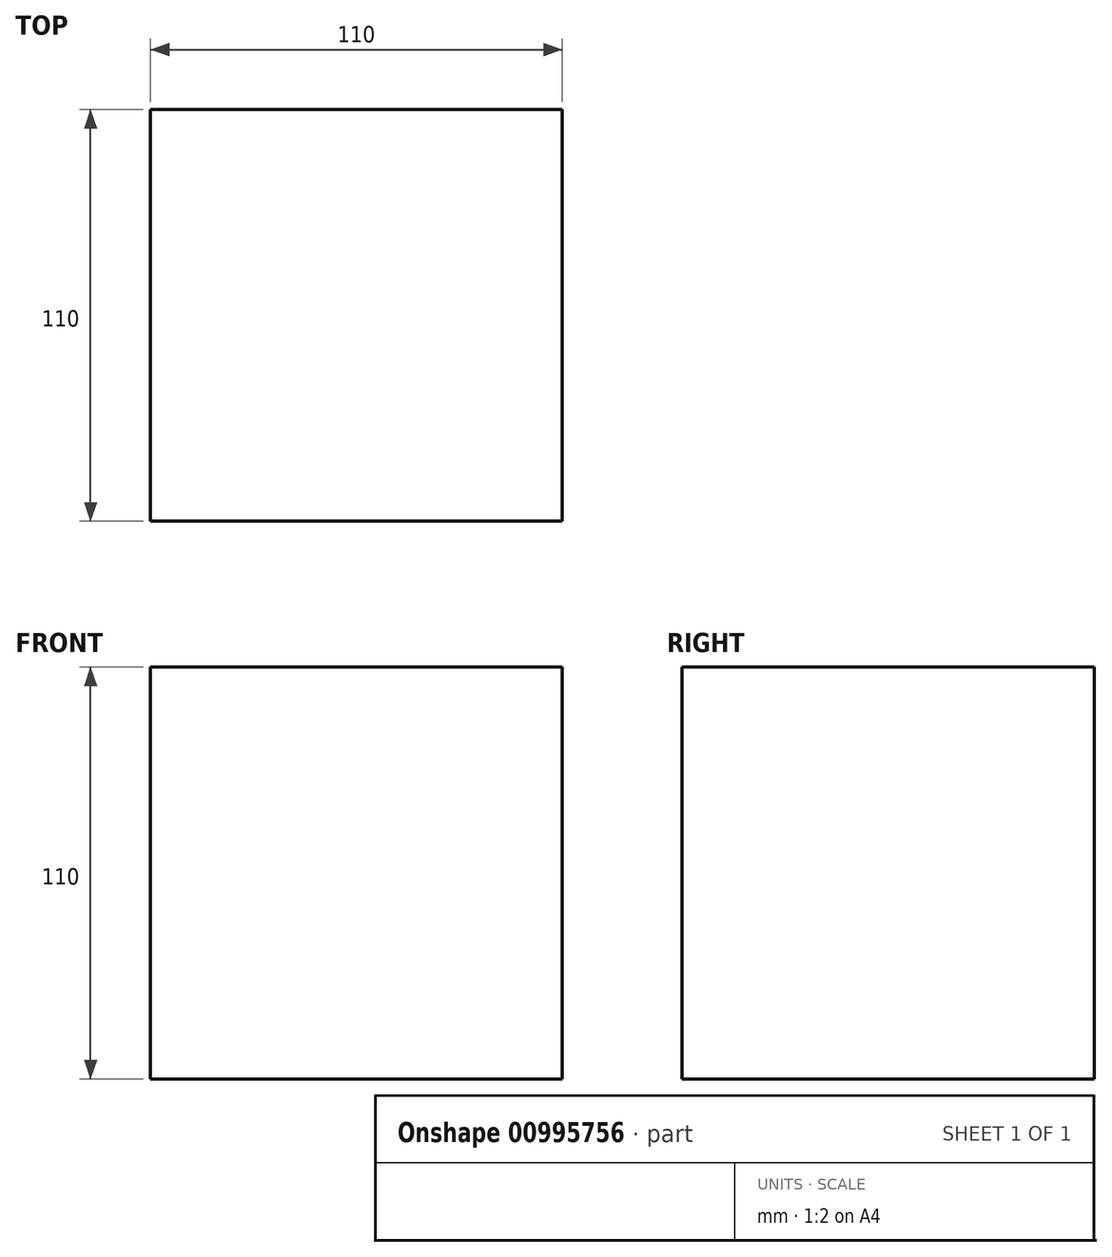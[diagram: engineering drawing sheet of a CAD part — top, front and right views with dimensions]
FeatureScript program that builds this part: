
annotation { "Feature Type Name" : "Feature", "Feature Type Description" : "" }
export const myFeature = defineFeature(function(context is Context, id is Id, definition is map)
    precondition{}
    {
        {
            var Q0;
            Q0=qCreatedBy(makeId("Top.planeOp"),FACE);
            var sketch = newSketch(context, id + "F0", { "sketchPlane" : qUnion([Q0])});
            skLineSegment(sketch, "E0.bottom", {"start": v(55, -55) * mm, "end": v(-55, -55) * mm});
            skLineSegment(sketch, "E0.top", {"start": v(55, 55) * mm, "end": v(-55, 55) * mm});
            skLineSegment(sketch, "E0.left", {"start": v(55, -55) * mm, "end": v(55, 55) * mm});
            skLineSegment(sketch, "E0.right", {"start": v(-55, -55) * mm, "end": v(-55, 55) * mm});
            skPoint(sketch, "E0.middle", {"position": v(0, 0) * mm});
            skSolve(sketch);
        }
        {
            var Q0;
            Q0 = qSketchRegion(id + "F0", true);
            extrude(context, id + "F1", {"entities" : qUnion([Q0]), "depth" : 110 * mm, "offsetDistance" : 25 * mm});
        }
    });
